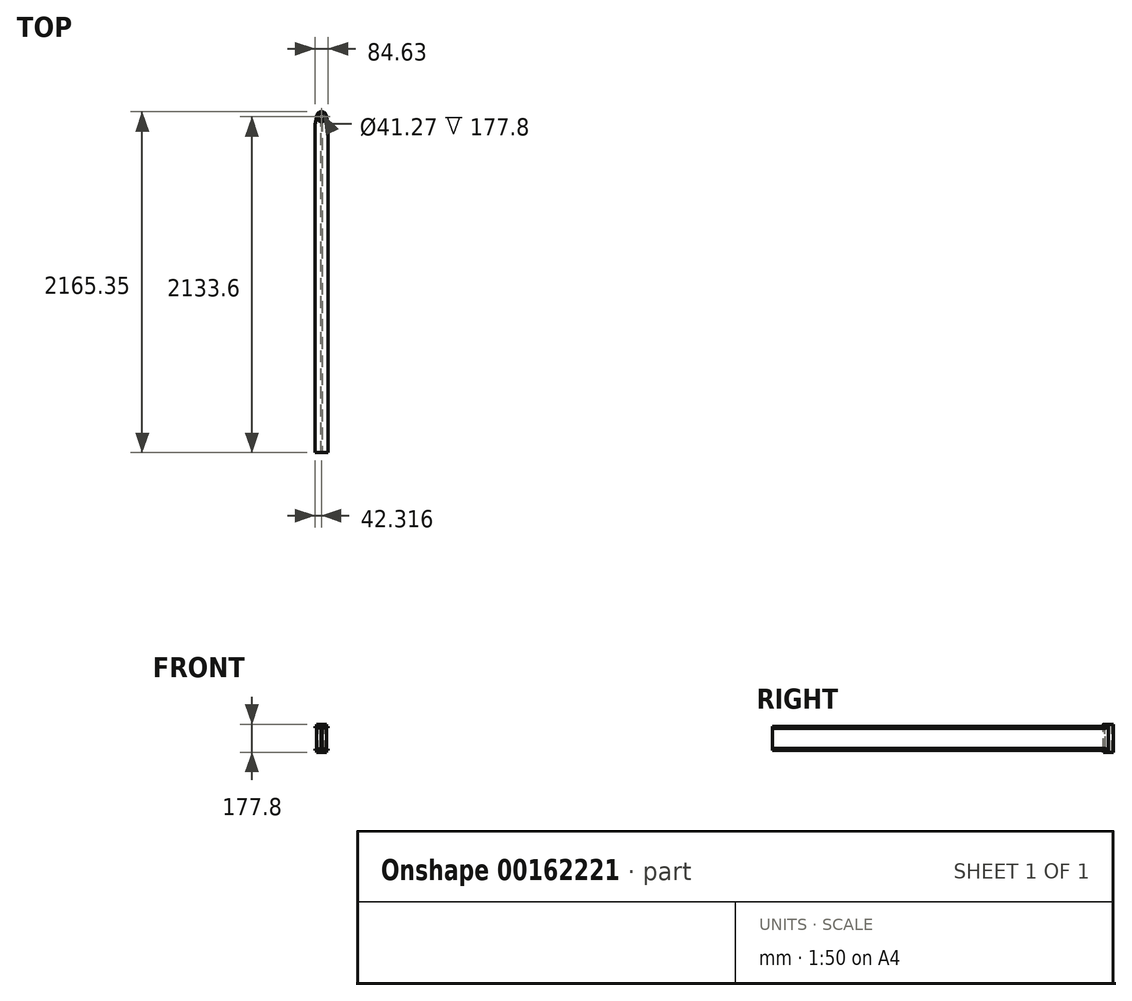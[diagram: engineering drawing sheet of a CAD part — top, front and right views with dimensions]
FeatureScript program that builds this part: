
annotation { "Feature Type Name" : "Feature", "Feature Type Description" : "" }
export const myFeature = defineFeature(function(context is Context, id is Id, definition is map)
    precondition{}
    {
        {
            var Q0;
            Q0=qCreatedBy(makeId("Front.planeOp"),FACE);
            var sketch = newSketch(context, id + "F0", { "sketchPlane" : qUnion([Q0])});
            skLineSegment(sketch, "E0.top", {"start": v(0, 143.28) * mm, "end": v(39.37, 143.28) * mm});
            skLineSegment(sketch, "E0.left", {"start": v(0, 134.16) * mm, "end": v(0, 143.28) * mm});
            skLineSegment(sketch, "E0.right", {"start": v(84.63, 134.16) * mm, "end": v(84.63, 143.28) * mm});
            skLineSegment(sketch, "E1.left", {"start": v(39.37, 134.16) * mm, "end": v(39.37, 0) * mm});
            skLineSegment(sketch, "E1.right", {"start": v(45.26, 134.16) * mm, "end": v(45.26, 0) * mm});
            skLineSegment(sketch, "E2.top", {"start": v(0, 134.16) * mm, "end": v(39.37, 134.16) * mm});
            skLineSegment(sketch, "E2.left", {"start": v(0, 143.28) * mm, "end": v(0, 134.16) * mm});
            skLineSegment(sketch, "E2.right", {"start": v(84.63, 143.28) * mm, "end": v(84.63, 134.16) * mm});
            skLineSegment(sketch, "E3.trimOffspring", {"start": v(45.26, 134.16) * mm, "end": v(84.63, 134.16) * mm});
            skLineSegment(sketch, "E4.trimOffspring", {"start": v(45.26, 143.28) * mm, "end": v(84.63, 143.28) * mm});
            skLineSegment(sketch, "E5", {"start": v(39.37, 143.28) * mm, "end": v(45.26, 143.28) * mm});
            skLineSegment(sketch, "E6.bottom", {"start": v(0, 0) * mm, "end": v(39.37, 0) * mm});
            skLineSegment(sketch, "E6.top", {"start": v(0, -9.12) * mm, "end": v(84.63, -9.12) * mm});
            skLineSegment(sketch, "E6.left", {"start": v(0, 0) * mm, "end": v(0, -9.12) * mm});
            skLineSegment(sketch, "E6.right", {"start": v(84.63, 0) * mm, "end": v(84.63, -9.12) * mm});
            skLineSegment(sketch, "E7.trimOffspring", {"start": v(45.26, 0) * mm, "end": v(84.63, 0) * mm});
            skSolve(sketch);
        }
        {
            var Q0;
            Q0=makeQuery(id+"F0.imprint","IMPRINT",FACE,{"disambiguationData":[TD([[makeQuery(id+"F0.imprint","IMPRINT",EDGE,{"derivedFrom":sQuery(id+"F0.wireOp",EDGE,"E1.left")}),1.0]])]});
            extrude(context, id + "F1", {"entities" : qUnion([Q0]), "endBound" : BoundingType.SYMMETRIC, "depth" : 2133.6 * mm});
        }
        {
            var Q0;
            Q0=makeQuery(id+"F1.opExtrude","SWEPT_EDGE",EDGE,{"disambiguationData":[OSD([sQuery(id+"F0.wireOp",EDGE,"E1.left"),sQuery(id+"F0.wireOp",EDGE,"E2.top")])]});
            var Q1;
            Q1=makeQuery(id+"F1.opExtrude","SWEPT_EDGE",EDGE,{"disambiguationData":[OSD([sQuery(id+"F0.wireOp",EDGE,"E1.right"),sQuery(id+"F0.wireOp",EDGE,"E7.trimOffspring")])]});
            chamfer(context, id + "F2", {"entities" : qUnion([Q0, Q1]), "chamferType" : ChamferType.OFFSET_ANGLE, "width" : 3.45 * mm, "oppositeDirection" : false, "angle" : 85 * degree, "tangentPropagation" : true});
        }
        {
            var Q0;
            Q0=makeQuery(id+"F1.opExtrude","SWEPT_EDGE",EDGE,{"disambiguationData":[OSD([sQuery(id+"F0.wireOp",EDGE,"E1.left"),sQuery(id+"F0.wireOp",EDGE,"E6.bottom")])]});
            var Q1;
            Q1=makeQuery(id+"F1.opExtrude","SWEPT_EDGE",EDGE,{"disambiguationData":[OSD([sQuery(id+"F0.wireOp",EDGE,"E1.right"),sQuery(id+"F0.wireOp",EDGE,"E3.trimOffspring")])]});
            chamfer(context, id + "F3", {"entities" : qUnion([Q0, Q1]), "chamferType" : ChamferType.OFFSET_ANGLE, "width" : 3.45 * mm, "oppositeDirection" : true, "angle" : 85 * degree, "tangentPropagation" : true});
        }
        {
            var Q0;
            Q0=makeQuery(id+"F1.opExtrude","SWEPT_FACE",FACE,{"disambiguationData":[OSD([sQuery(id+"F0.wireOp",EDGE,"E0.top"),sQuery(id+"F0.wireOp",EDGE,"E4.trimOffspring"),sQuery(id+"F0.wireOp",EDGE,"E5")])]});
            var sketch = newSketch(context, id + "F4", { "sketchPlane" : qUnion([Q0])});
            skCircle(sketch, "E8", {"center": v(42.32, 1066.8) * mm, "radius": 31.75 * mm});
            skCircle(sketch, "E9", {"center": v(42.32, 1066.8) * mm, "radius": 20.64 * mm});
            skSolve(sketch);
        }
        {
            var Q0;
            {var subQ0=sQuery(id+"F4.wireOp",EDGE,"E8");var subQ1=makeQuery(id+"F1.opExtrude","CAP_EDGE",EDGE,{"disambiguationData":[OSD([sQuery(id+"F0.wireOp",EDGE,"E0.top"),sQuery(id+"F0.wireOp",EDGE,"E4.trimOffspring"),sQuery(id+"F0.wireOp",EDGE,"E5")])],"isStart":true});var subQ2=makeQuery(id+"F4.imprint","INTERSECT",VERTEX,{"disambiguationData":[OD(0.0)],"derivedFrom":[subQ1,subQ0]});Q0=makeQuery(id+"F4.imprint","IMPRINT",FACE,{"disambiguationData":[TD([[makeQuery(id+"F4.imprint","IMPRINT",EDGE,{"disambiguationData":[TD([[subQ2,1.0]])],"derivedFrom":subQ0}),1.0]])]});}
            var Q1;
            {var subQ0=sQuery(id+"F4.wireOp",EDGE,"E8");var subQ1=makeQuery(id+"F1.opExtrude","CAP_EDGE",EDGE,{"disambiguationData":[OSD([sQuery(id+"F0.wireOp",EDGE,"E0.top"),sQuery(id+"F0.wireOp",EDGE,"E4.trimOffspring"),sQuery(id+"F0.wireOp",EDGE,"E5")])],"isStart":true});var subQ2=makeQuery(id+"F4.imprint","INTERSECT",VERTEX,{"disambiguationData":[OD(0.0)],"derivedFrom":[subQ1,subQ0]});Q1=makeQuery(id+"F4.imprint","IMPRINT",FACE,{"disambiguationData":[TD([[makeQuery(id+"F4.imprint","IMPRINT",EDGE,{"disambiguationData":[TD([[subQ2,-1.0]])],"derivedFrom":subQ0}),1.0]])]});}
            extrude(context, id + "F5", {"entities" : qUnion([Q0, Q1]), "oppositeDirection" : true, "depth" : 165.1 * mm, "hasSecondDirection" : true, "secondDirectionOppositeDirection" : false, "secondDirectionDepth" : 12.7 * mm});
        }
        {
            var Q0;
            Q0=makeQuery(id+"F1.opExtrude","SWEPT_FACE",FACE,{"disambiguationData":[OSD([sQuery(id+"F0.wireOp",EDGE,"E0.top"),sQuery(id+"F0.wireOp",EDGE,"E4.trimOffspring"),sQuery(id+"F0.wireOp",EDGE,"E5")])]});
            var sketch = newSketch(context, id + "F6", { "sketchPlane" : qUnion([Q0])});
            skCircle(sketch, "E10", {"center": v(42.32, 1066.8) * mm, "radius": 20.64 * mm});
            skSolve(sketch);
        }
        {
            var Q0;
            Q0 = qSketchRegion(id + "F6", true);
            extrude(context, id + "F7", {"entities" : qUnion([Q0]), "operationType" : NewBodyOperationType.REMOVE, "endBound" : BoundingType.THROUGH_ALL, "oppositeDirection" : true, "depth" : 25.4 * mm});
        }
        {
            var Q0;
            Q0=makeQuery(id+"F1.opExtrude","SWEPT_FACE",FACE,{"disambiguationData":[OSD([sQuery(id+"F0.wireOp",EDGE,"E0.top"),sQuery(id+"F0.wireOp",EDGE,"E4.trimOffspring"),sQuery(id+"F0.wireOp",EDGE,"E5")])]});
            var sketch = newSketch(context, id + "F8", { "sketchPlane" : qUnion([Q0])});
            skLineSegment(sketch, "E11", {"start": v(10.84, 1066.8) * mm, "end": v(0, 1016) * mm});
            skLineSegment(sketch, "E12", {"start": v(0, 1016) * mm, "end": v(0, 1066.8) * mm});
            skLineSegment(sketch, "E13", {"start": v(0, 1066.8) * mm, "end": v(10.84, 1066.8) * mm});
            skLineSegment(sketch, "E14", {"start": v(84.63, 1066.8) * mm, "end": v(73.8, 1066.8) * mm});
            skLineSegment(sketch, "E15", {"start": v(73.8, 1066.8) * mm, "end": v(84.63, 1016) * mm});
            skLineSegment(sketch, "E16", {"start": v(84.63, 1016) * mm, "end": v(84.63, 1066.8) * mm});
            skSolve(sketch);
        }
        {
            var Q0;
            Q0 = qSketchRegion(id + "F8", true);
            extrude(context, id + "F9", {"entities" : qUnion([Q0]), "operationType" : NewBodyOperationType.REMOVE, "endBound" : BoundingType.THROUGH_ALL, "oppositeDirection" : true, "depth" : 25.4 * mm});
        }
    });
